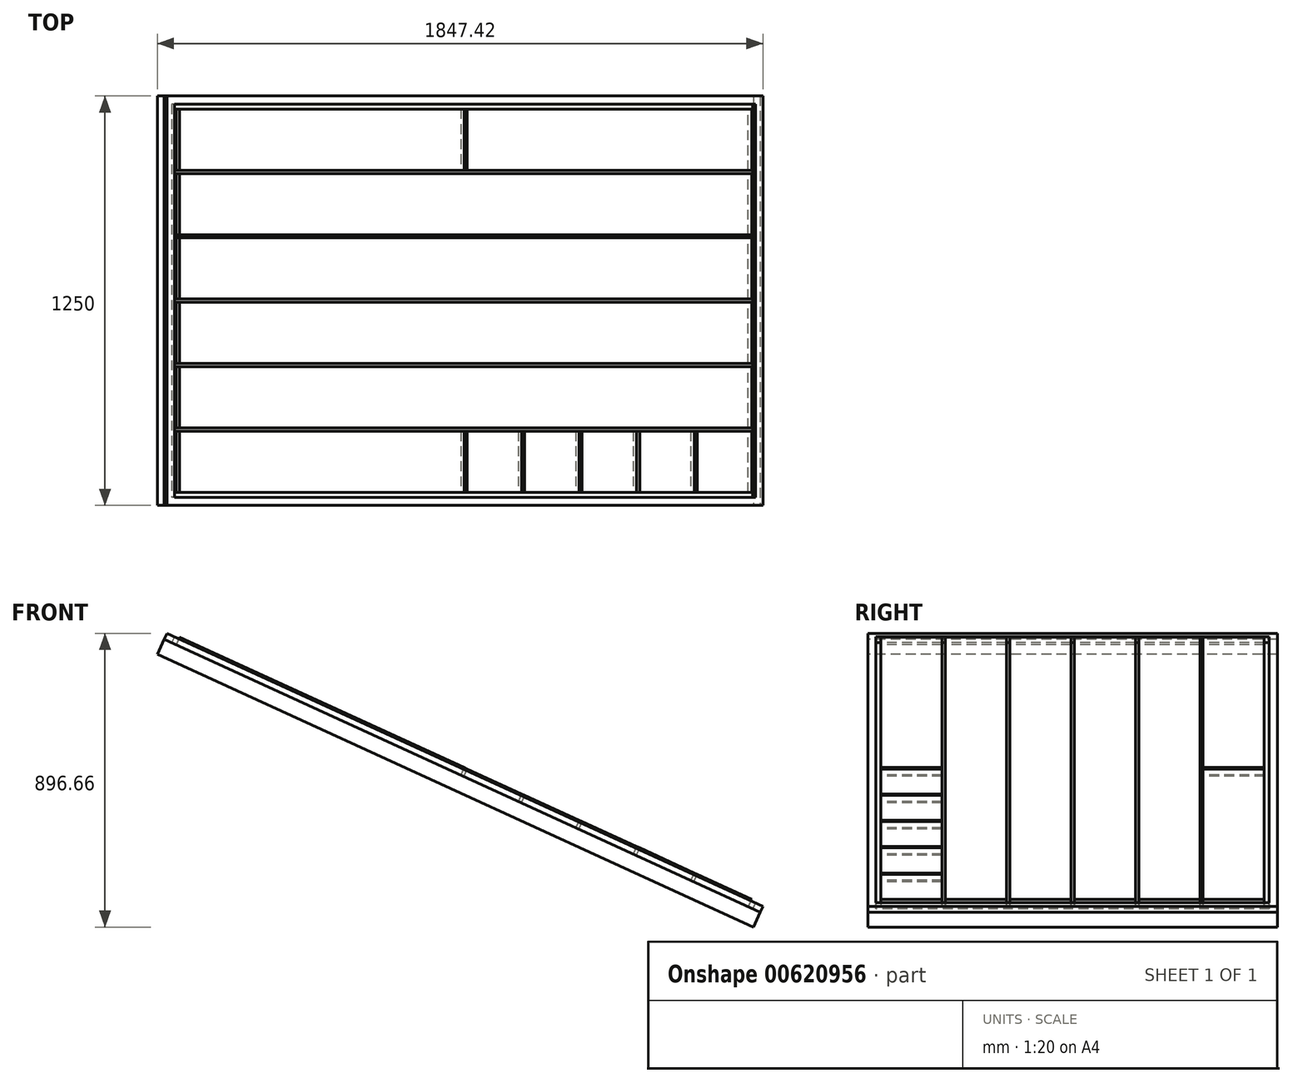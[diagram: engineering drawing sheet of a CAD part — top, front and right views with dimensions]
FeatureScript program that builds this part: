
annotation { "Feature Type Name" : "Feature", "Feature Type Description" : "" }
export const myFeature = defineFeature(function(context is Context, id is Id, definition is map)
    precondition{}
    {
        {
            var Q0;
            Q0=qCreatedBy(makeId("Front.planeOp"),FACE);
            var sketch = newSketch(context, id + "F0", { "sketchPlane" : qUnion([Q0])});
            skLineSegment(sketch, "E0", {"start": v(0, 0) * mm, "end": v(-1818.26, 833.02) * mm});
            skLineSegment(sketch, "E1.0", {"start": v(20.83, 45.46) * mm, "end": v(-1797.44, 878.48) * mm});
            skLineSegment(sketch, "E2", {"start": v(-1818.26, 833.02) * mm, "end": v(-1797.44, 878.48) * mm});
            skLineSegment(sketch, "E3", {"start": v(0, 0) * mm, "end": v(20.83, 45.46) * mm});
            skSolve(sketch);
        }
        {
            var Q0;
            Q0 = qSketchRegion(id + "F0", true);
            extrude(context, id + "F1", {"entities" : qUnion([Q0]), "oppositeDirection" : true, "depth" : 1250 * mm, "offsetDistance" : 25 * mm});
        }
        {
            var Q0;
            Q0=makeQuery(id+"F1.opExtrude","SWEPT_FACE",FACE,{"disambiguationData":[OSD([sQuery(id+"F0.wireOp",EDGE,"E1.0")])]});
            var sketch = newSketch(context, id + "F2", { "sketchPlane" : qUnion([Q0])});
            skLineSegment(sketch, "E4.0.0", {"start": v(-2000, 0) * mm, "end": v(0, 0) * mm});
            skLineSegment(sketch, "E4.0.1", {"start": v(0, 0) * mm, "end": v(0, 1250) * mm});
            skLineSegment(sketch, "E4.0.2", {"start": v(0, 1250) * mm, "end": v(-2000, 1250) * mm});
            skLineSegment(sketch, "E4.0.3", {"start": v(-2000, 1250) * mm, "end": v(-2000, 0) * mm});
            skLineSegment(sketch, "E5.0", {"start": v(-1960, 1210) * mm, "end": v(-1960, 1023.32) * mm});
            skLineSegment(sketch, "E5.1", {"start": v(-40, 1210) * mm, "end": v(-995, 1210) * mm});
            skLineSegment(sketch, "E5.2", {"start": v(-40, 40) * mm, "end": v(-40, 226.68) * mm});
            skLineSegment(sketch, "E5.3", {"start": v(-1960, 40) * mm, "end": v(-1005, 40) * mm});
            skLineSegment(sketch, "E6.0", {"start": v(-40, 630) * mm, "end": v(-1960, 630) * mm});
            skLineSegment(sketch, "E7.0", {"start": v(-40, 620) * mm, "end": v(-1960, 620) * mm});
            skLineSegment(sketch, "E8.trimOffspring", {"start": v(-1960, 620) * mm, "end": v(-1960, 433.34) * mm});
            skLineSegment(sketch, "E9.trimOffspring", {"start": v(-40, 630) * mm, "end": v(-40, 816.66) * mm});
            skLineSegment(sketch, "E10.0", {"start": v(-40, 816.66) * mm, "end": v(-1960, 816.66) * mm});
            skLineSegment(sketch, "E11.0", {"start": v(-40, 826.66) * mm, "end": v(-1960, 826.66) * mm});
            skLineSegment(sketch, "E12.0", {"start": v(-40, 1013.32) * mm, "end": v(-1960, 1013.32) * mm});
            skLineSegment(sketch, "E13.0", {"start": v(-40, 1023.32) * mm, "end": v(-1960, 1023.32) * mm});
            skLineSegment(sketch, "E14", {"start": v(-2000, 625) * mm, "end": v(-2336.37, 625) * mm, "construction": true});
            skLineSegment(sketch, "E15.MirrorCS", {"start": v(-40, 226.68) * mm, "end": v(-1960, 226.68) * mm});
            skLineSegment(sketch, "E16.MirrorCS", {"start": v(-40, 236.68) * mm, "end": v(-1960, 236.68) * mm});
            skLineSegment(sketch, "E17.MirrorCS", {"start": v(-40, 423.34) * mm, "end": v(-1960, 423.34) * mm});
            skLineSegment(sketch, "E18.MirrorCS", {"start": v(-40, 433.34) * mm, "end": v(-1960, 433.34) * mm});
            skLineSegment(sketch, "E19.trimOffspring", {"start": v(-1960, 1013.32) * mm, "end": v(-1960, 826.66) * mm});
            skLineSegment(sketch, "E20.trimOffspring", {"start": v(-1960, 816.66) * mm, "end": v(-1960, 630) * mm});
            skLineSegment(sketch, "E21.trimOffspring", {"start": v(-1960, 423.34) * mm, "end": v(-1960, 236.68) * mm});
            skLineSegment(sketch, "E22.trimOffspring", {"start": v(-1960, 226.68) * mm, "end": v(-1960, 40) * mm});
            skLineSegment(sketch, "E23.trimOffspring", {"start": v(-40, 236.68) * mm, "end": v(-40, 423.34) * mm});
            skLineSegment(sketch, "E24.trimOffspring", {"start": v(-40, 433.34) * mm, "end": v(-40, 620) * mm});
            skLineSegment(sketch, "E25.trimOffspring", {"start": v(-40, 826.66) * mm, "end": v(-40, 1013.32) * mm});
            skLineSegment(sketch, "E26.trimOffspring", {"start": v(-40, 1023.32) * mm, "end": v(-40, 1210) * mm});
            skLineSegment(sketch, "E27.0", {"start": v(-1005, 1210) * mm, "end": v(-1005, 40) * mm});
            skLineSegment(sketch, "E28.0", {"start": v(-995, 1210) * mm, "end": v(-995, 40) * mm});
            skLineSegment(sketch, "E29.trimOffspring", {"start": v(-995, 40) * mm, "end": v(-40, 40) * mm});
            skLineSegment(sketch, "E30.trimOffspring", {"start": v(-1005, 1210) * mm, "end": v(-1960, 1210) * mm});
            skLineSegment(sketch, "E31.0", {"start": v(-1188, 1210) * mm, "end": v(-1188, 40) * mm});
            skLineSegment(sketch, "E32.0", {"start": v(-1198, 1210) * mm, "end": v(-1198, 40) * mm});
            skLineSegment(sketch, "E33.0", {"start": v(-1381, 1210) * mm, "end": v(-1381, 40) * mm});
            skLineSegment(sketch, "E34.0", {"start": v(-1391, 1210) * mm, "end": v(-1391, 40) * mm});
            skLineSegment(sketch, "E35.0", {"start": v(-1574, 1210) * mm, "end": v(-1574, 40) * mm});
            skLineSegment(sketch, "E36.0", {"start": v(-1584, 1210) * mm, "end": v(-1584, 40) * mm});
            skLineSegment(sketch, "E37.0", {"start": v(-1767, 1210) * mm, "end": v(-1767, 40) * mm});
            skLineSegment(sketch, "E38.0", {"start": v(-1777, 1210) * mm, "end": v(-1777, 40) * mm});
            skLineSegment(sketch, "E39", {"start": v(-1000, 0) * mm, "end": v(-1000, -135.03) * mm, "construction": true});
            skLineSegment(sketch, "E40.MirrorCS", {"start": v(-619, 1210) * mm, "end": v(-619, 40) * mm});
            skLineSegment(sketch, "E41.MirrorCS", {"start": v(-802, 1210) * mm, "end": v(-802, 40) * mm});
            skLineSegment(sketch, "E42.MirrorCS", {"start": v(-233, 1210) * mm, "end": v(-233, 40) * mm});
            skLineSegment(sketch, "E43.MirrorCS", {"start": v(-609, 1210) * mm, "end": v(-609, 40) * mm});
            skLineSegment(sketch, "E44.MirrorCS", {"start": v(-416, 1210) * mm, "end": v(-416, 40) * mm});
            skLineSegment(sketch, "E45.MirrorCS", {"start": v(-426, 1210) * mm, "end": v(-426, 40) * mm});
            skLineSegment(sketch, "E46.MirrorCS", {"start": v(-812, 1210) * mm, "end": v(-812, 40) * mm});
            skLineSegment(sketch, "E47.MirrorCS", {"start": v(-223, 1210) * mm, "end": v(-223, 40) * mm});
            skSolve(sketch);
        }
        {
            var Q0;
            {var subQ0=sQuery(id+"F2.wireOp",EDGE,"E22.trimOffspring");Q0=makeQuery(id+"F2.imprint","IMPRINT",FACE,{"disambiguationData":[TD([[makeQuery(id+"F2.imprint","IMPRINT",EDGE,{"derivedFrom":subQ0}),1.0]])]});}
            var Q1;
            {var subQ0=sQuery(id+"F2.wireOp",EDGE,"E21.trimOffspring");Q1=makeQuery(id+"F2.imprint","IMPRINT",FACE,{"disambiguationData":[TD([[makeQuery(id+"F2.imprint","IMPRINT",EDGE,{"derivedFrom":subQ0}),1.0]])]});}
            var Q2;
            {var subQ0=sQuery(id+"F2.wireOp",EDGE,"E8.trimOffspring");Q2=makeQuery(id+"F2.imprint","IMPRINT",FACE,{"disambiguationData":[TD([[makeQuery(id+"F2.imprint","IMPRINT",EDGE,{"derivedFrom":subQ0}),1.0]])]});}
            var Q3;
            {var subQ0=sQuery(id+"F2.wireOp",EDGE,"E20.trimOffspring");Q3=makeQuery(id+"F2.imprint","IMPRINT",FACE,{"disambiguationData":[TD([[makeQuery(id+"F2.imprint","IMPRINT",EDGE,{"derivedFrom":subQ0}),1.0]])]});}
            var Q4;
            {var subQ0=sQuery(id+"F2.wireOp",EDGE,"E19.trimOffspring");Q4=makeQuery(id+"F2.imprint","IMPRINT",FACE,{"disambiguationData":[TD([[makeQuery(id+"F2.imprint","IMPRINT",EDGE,{"derivedFrom":subQ0}),1.0]])]});}
            var Q5;
            {var subQ0=sQuery(id+"F2.wireOp",EDGE,"E5.0");Q5=makeQuery(id+"F2.imprint","IMPRINT",FACE,{"disambiguationData":[TD([[makeQuery(id+"F2.imprint","IMPRINT",EDGE,{"derivedFrom":subQ0}),1.0]])]});}
            var Q6;
            {var subQ0=sQuery(id+"F2.wireOp",EDGE,"E36.0");var subQ1=sQuery(id+"F2.wireOp",EDGE,"E5.3");var subQ2=makeQuery(id+"F2.imprint","INTERSECT",VERTEX,{"derivedFrom":[subQ1,subQ0]});Q6=makeQuery(id+"F2.imprint","IMPRINT",FACE,{"disambiguationData":[TD([[makeQuery(id+"F2.imprint","IMPRINT",EDGE,{"disambiguationData":[TD([[subQ2,1.0]])],"derivedFrom":subQ1}),1.0]])]});}
            var Q7;
            {var subQ0=sQuery(id+"F2.wireOp",EDGE,"E36.0");var subQ1=sQuery(id+"F2.wireOp",EDGE,"E16.MirrorCS");var subQ2=makeQuery(id+"F2.imprint","INTERSECT",VERTEX,{"derivedFrom":[subQ1,subQ0]});Q7=makeQuery(id+"F2.imprint","IMPRINT",FACE,{"disambiguationData":[TD([[makeQuery(id+"F2.imprint","IMPRINT",EDGE,{"disambiguationData":[TD([[subQ2,-1.0]])],"derivedFrom":subQ1}),-1.0]])]});}
            var Q8;
            {var subQ0=sQuery(id+"F2.wireOp",EDGE,"E36.0");var subQ1=sQuery(id+"F2.wireOp",EDGE,"E7.0");var subQ2=makeQuery(id+"F2.imprint","INTERSECT",VERTEX,{"derivedFrom":[subQ1,subQ0]});Q8=makeQuery(id+"F2.imprint","IMPRINT",FACE,{"disambiguationData":[TD([[makeQuery(id+"F2.imprint","IMPRINT",EDGE,{"disambiguationData":[TD([[subQ2,-1.0]])],"derivedFrom":subQ1}),1.0]])]});}
            var Q9;
            {var subQ0=sQuery(id+"F2.wireOp",EDGE,"E36.0");var subQ1=sQuery(id+"F2.wireOp",EDGE,"E6.0");var subQ2=makeQuery(id+"F2.imprint","INTERSECT",VERTEX,{"derivedFrom":[subQ1,subQ0]});Q9=makeQuery(id+"F2.imprint","IMPRINT",FACE,{"disambiguationData":[TD([[makeQuery(id+"F2.imprint","IMPRINT",EDGE,{"disambiguationData":[TD([[subQ2,-1.0]])],"derivedFrom":subQ1}),-1.0]])]});}
            var Q10;
            {var subQ0=sQuery(id+"F2.wireOp",EDGE,"E36.0");var subQ1=sQuery(id+"F2.wireOp",EDGE,"E11.0");var subQ2=makeQuery(id+"F2.imprint","INTERSECT",VERTEX,{"derivedFrom":[subQ1,subQ0]});Q10=makeQuery(id+"F2.imprint","IMPRINT",FACE,{"disambiguationData":[TD([[makeQuery(id+"F2.imprint","IMPRINT",EDGE,{"disambiguationData":[TD([[subQ2,-1.0]])],"derivedFrom":subQ1}),-1.0]])]});}
            var Q11;
            {var subQ0=sQuery(id+"F2.wireOp",EDGE,"E36.0");var subQ1=sQuery(id+"F2.wireOp",EDGE,"E13.0");var subQ2=makeQuery(id+"F2.imprint","INTERSECT",VERTEX,{"derivedFrom":[subQ1,subQ0]});Q11=makeQuery(id+"F2.imprint","IMPRINT",FACE,{"disambiguationData":[TD([[makeQuery(id+"F2.imprint","IMPRINT",EDGE,{"disambiguationData":[TD([[subQ2,-1.0]])],"derivedFrom":subQ1}),-1.0]])]});}
            var Q12;
            {var subQ0=sQuery(id+"F2.wireOp",EDGE,"E34.0");var subQ1=sQuery(id+"F2.wireOp",EDGE,"E13.0");var subQ2=makeQuery(id+"F2.imprint","INTERSECT",VERTEX,{"derivedFrom":[subQ1,subQ0]});Q12=makeQuery(id+"F2.imprint","IMPRINT",FACE,{"disambiguationData":[TD([[makeQuery(id+"F2.imprint","IMPRINT",EDGE,{"disambiguationData":[TD([[subQ2,-1.0]])],"derivedFrom":subQ1}),-1.0]])]});}
            var Q13;
            {var subQ0=sQuery(id+"F2.wireOp",EDGE,"E34.0");var subQ1=sQuery(id+"F2.wireOp",EDGE,"E11.0");var subQ2=makeQuery(id+"F2.imprint","INTERSECT",VERTEX,{"derivedFrom":[subQ1,subQ0]});Q13=makeQuery(id+"F2.imprint","IMPRINT",FACE,{"disambiguationData":[TD([[makeQuery(id+"F2.imprint","IMPRINT",EDGE,{"disambiguationData":[TD([[subQ2,-1.0]])],"derivedFrom":subQ1}),-1.0]])]});}
            var Q14;
            {var subQ0=sQuery(id+"F2.wireOp",EDGE,"E34.0");var subQ1=sQuery(id+"F2.wireOp",EDGE,"E6.0");var subQ2=makeQuery(id+"F2.imprint","INTERSECT",VERTEX,{"derivedFrom":[subQ1,subQ0]});Q14=makeQuery(id+"F2.imprint","IMPRINT",FACE,{"disambiguationData":[TD([[makeQuery(id+"F2.imprint","IMPRINT",EDGE,{"disambiguationData":[TD([[subQ2,-1.0]])],"derivedFrom":subQ1}),-1.0]])]});}
            var Q15;
            {var subQ0=sQuery(id+"F2.wireOp",EDGE,"E34.0");var subQ1=sQuery(id+"F2.wireOp",EDGE,"E7.0");var subQ2=makeQuery(id+"F2.imprint","INTERSECT",VERTEX,{"derivedFrom":[subQ1,subQ0]});Q15=makeQuery(id+"F2.imprint","IMPRINT",FACE,{"disambiguationData":[TD([[makeQuery(id+"F2.imprint","IMPRINT",EDGE,{"disambiguationData":[TD([[subQ2,-1.0]])],"derivedFrom":subQ1}),1.0]])]});}
            var Q16;
            {var subQ0=sQuery(id+"F2.wireOp",EDGE,"E34.0");var subQ1=sQuery(id+"F2.wireOp",EDGE,"E16.MirrorCS");var subQ2=makeQuery(id+"F2.imprint","INTERSECT",VERTEX,{"derivedFrom":[subQ1,subQ0]});Q16=makeQuery(id+"F2.imprint","IMPRINT",FACE,{"disambiguationData":[TD([[makeQuery(id+"F2.imprint","IMPRINT",EDGE,{"disambiguationData":[TD([[subQ2,-1.0]])],"derivedFrom":subQ1}),-1.0]])]});}
            var Q17;
            {var subQ0=sQuery(id+"F2.wireOp",EDGE,"E34.0");var subQ1=sQuery(id+"F2.wireOp",EDGE,"E5.3");var subQ2=makeQuery(id+"F2.imprint","INTERSECT",VERTEX,{"derivedFrom":[subQ1,subQ0]});Q17=makeQuery(id+"F2.imprint","IMPRINT",FACE,{"disambiguationData":[TD([[makeQuery(id+"F2.imprint","IMPRINT",EDGE,{"disambiguationData":[TD([[subQ2,1.0]])],"derivedFrom":subQ1}),1.0]])]});}
            var Q18;
            {var subQ0=sQuery(id+"F2.wireOp",EDGE,"E32.0");var subQ1=sQuery(id+"F2.wireOp",EDGE,"E5.3");var subQ2=makeQuery(id+"F2.imprint","INTERSECT",VERTEX,{"derivedFrom":[subQ1,subQ0]});Q18=makeQuery(id+"F2.imprint","IMPRINT",FACE,{"disambiguationData":[TD([[makeQuery(id+"F2.imprint","IMPRINT",EDGE,{"disambiguationData":[TD([[subQ2,1.0]])],"derivedFrom":subQ1}),1.0]])]});}
            var Q19;
            {var subQ0=sQuery(id+"F2.wireOp",EDGE,"E32.0");var subQ1=sQuery(id+"F2.wireOp",EDGE,"E16.MirrorCS");var subQ2=makeQuery(id+"F2.imprint","INTERSECT",VERTEX,{"derivedFrom":[subQ1,subQ0]});Q19=makeQuery(id+"F2.imprint","IMPRINT",FACE,{"disambiguationData":[TD([[makeQuery(id+"F2.imprint","IMPRINT",EDGE,{"disambiguationData":[TD([[subQ2,-1.0]])],"derivedFrom":subQ1}),-1.0]])]});}
            var Q20;
            {var subQ0=sQuery(id+"F2.wireOp",EDGE,"E32.0");var subQ1=sQuery(id+"F2.wireOp",EDGE,"E7.0");var subQ2=makeQuery(id+"F2.imprint","INTERSECT",VERTEX,{"derivedFrom":[subQ1,subQ0]});Q20=makeQuery(id+"F2.imprint","IMPRINT",FACE,{"disambiguationData":[TD([[makeQuery(id+"F2.imprint","IMPRINT",EDGE,{"disambiguationData":[TD([[subQ2,-1.0]])],"derivedFrom":subQ1}),1.0]])]});}
            var Q21;
            {var subQ0=sQuery(id+"F2.wireOp",EDGE,"E32.0");var subQ1=sQuery(id+"F2.wireOp",EDGE,"E6.0");var subQ2=makeQuery(id+"F2.imprint","INTERSECT",VERTEX,{"derivedFrom":[subQ1,subQ0]});Q21=makeQuery(id+"F2.imprint","IMPRINT",FACE,{"disambiguationData":[TD([[makeQuery(id+"F2.imprint","IMPRINT",EDGE,{"disambiguationData":[TD([[subQ2,-1.0]])],"derivedFrom":subQ1}),-1.0]])]});}
            var Q22;
            {var subQ0=sQuery(id+"F2.wireOp",EDGE,"E32.0");var subQ1=sQuery(id+"F2.wireOp",EDGE,"E11.0");var subQ2=makeQuery(id+"F2.imprint","INTERSECT",VERTEX,{"derivedFrom":[subQ1,subQ0]});Q22=makeQuery(id+"F2.imprint","IMPRINT",FACE,{"disambiguationData":[TD([[makeQuery(id+"F2.imprint","IMPRINT",EDGE,{"disambiguationData":[TD([[subQ2,-1.0]])],"derivedFrom":subQ1}),-1.0]])]});}
            var Q23;
            {var subQ0=sQuery(id+"F2.wireOp",EDGE,"E32.0");var subQ1=sQuery(id+"F2.wireOp",EDGE,"E13.0");var subQ2=makeQuery(id+"F2.imprint","INTERSECT",VERTEX,{"derivedFrom":[subQ1,subQ0]});Q23=makeQuery(id+"F2.imprint","IMPRINT",FACE,{"disambiguationData":[TD([[makeQuery(id+"F2.imprint","IMPRINT",EDGE,{"disambiguationData":[TD([[subQ2,-1.0]])],"derivedFrom":subQ1}),-1.0]])]});}
            var Q24;
            {var subQ0=sQuery(id+"F2.wireOp",EDGE,"E27.0");var subQ1=sQuery(id+"F2.wireOp",EDGE,"E5.3");var subQ2=makeQuery(id+"F2.imprint","INTERSECT",VERTEX,{"derivedFrom":[subQ1,subQ0]});Q24=makeQuery(id+"F2.imprint","IMPRINT",FACE,{"disambiguationData":[TD([[makeQuery(id+"F2.imprint","IMPRINT",EDGE,{"disambiguationData":[TD([[subQ2,1.0]])],"derivedFrom":subQ1}),1.0]])]});}
            var Q25;
            {var subQ0=sQuery(id+"F2.wireOp",EDGE,"E27.0");var subQ1=sQuery(id+"F2.wireOp",EDGE,"E16.MirrorCS");var subQ2=makeQuery(id+"F2.imprint","INTERSECT",VERTEX,{"derivedFrom":[subQ1,subQ0]});Q25=makeQuery(id+"F2.imprint","IMPRINT",FACE,{"disambiguationData":[TD([[makeQuery(id+"F2.imprint","IMPRINT",EDGE,{"disambiguationData":[TD([[subQ2,-1.0]])],"derivedFrom":subQ1}),-1.0]])]});}
            var Q26;
            {var subQ0=sQuery(id+"F2.wireOp",EDGE,"E27.0");var subQ1=sQuery(id+"F2.wireOp",EDGE,"E7.0");var subQ2=makeQuery(id+"F2.imprint","INTERSECT",VERTEX,{"derivedFrom":[subQ1,subQ0]});Q26=makeQuery(id+"F2.imprint","IMPRINT",FACE,{"disambiguationData":[TD([[makeQuery(id+"F2.imprint","IMPRINT",EDGE,{"disambiguationData":[TD([[subQ2,-1.0]])],"derivedFrom":subQ1}),1.0]])]});}
            var Q27;
            {var subQ0=sQuery(id+"F2.wireOp",EDGE,"E27.0");var subQ1=sQuery(id+"F2.wireOp",EDGE,"E6.0");var subQ2=makeQuery(id+"F2.imprint","INTERSECT",VERTEX,{"derivedFrom":[subQ1,subQ0]});Q27=makeQuery(id+"F2.imprint","IMPRINT",FACE,{"disambiguationData":[TD([[makeQuery(id+"F2.imprint","IMPRINT",EDGE,{"disambiguationData":[TD([[subQ2,-1.0]])],"derivedFrom":subQ1}),-1.0]])]});}
            var Q28;
            {var subQ0=sQuery(id+"F2.wireOp",EDGE,"E27.0");var subQ1=sQuery(id+"F2.wireOp",EDGE,"E11.0");var subQ2=makeQuery(id+"F2.imprint","INTERSECT",VERTEX,{"derivedFrom":[subQ1,subQ0]});Q28=makeQuery(id+"F2.imprint","IMPRINT",FACE,{"disambiguationData":[TD([[makeQuery(id+"F2.imprint","IMPRINT",EDGE,{"disambiguationData":[TD([[subQ2,-1.0]])],"derivedFrom":subQ1}),-1.0]])]});}
            var Q29;
            {var subQ0=sQuery(id+"F2.wireOp",EDGE,"E27.0");var subQ1=sQuery(id+"F2.wireOp",EDGE,"E13.0");var subQ2=makeQuery(id+"F2.imprint","INTERSECT",VERTEX,{"derivedFrom":[subQ1,subQ0]});Q29=makeQuery(id+"F2.imprint","IMPRINT",FACE,{"disambiguationData":[TD([[makeQuery(id+"F2.imprint","IMPRINT",EDGE,{"disambiguationData":[TD([[subQ2,-1.0]])],"derivedFrom":subQ1}),-1.0]])]});}
            var Q30;
            {var subQ0=sQuery(id+"F2.wireOp",EDGE,"E46.MirrorCS");var subQ1=sQuery(id+"F2.wireOp",EDGE,"E15.MirrorCS");var subQ2=makeQuery(id+"F2.imprint","INTERSECT",VERTEX,{"derivedFrom":[subQ1,subQ0]});Q30=makeQuery(id+"F2.imprint","IMPRINT",FACE,{"disambiguationData":[TD([[makeQuery(id+"F2.imprint","IMPRINT",EDGE,{"disambiguationData":[TD([[subQ2,-1.0]])],"derivedFrom":subQ1}),1.0]])]});}
            var Q31;
            {var subQ0=sQuery(id+"F2.wireOp",EDGE,"E46.MirrorCS");var subQ1=sQuery(id+"F2.wireOp",EDGE,"E16.MirrorCS");var subQ2=makeQuery(id+"F2.imprint","INTERSECT",VERTEX,{"derivedFrom":[subQ1,subQ0]});Q31=makeQuery(id+"F2.imprint","IMPRINT",FACE,{"disambiguationData":[TD([[makeQuery(id+"F2.imprint","IMPRINT",EDGE,{"disambiguationData":[TD([[subQ2,-1.0]])],"derivedFrom":subQ1}),-1.0]])]});}
            var Q32;
            {var subQ0=sQuery(id+"F2.wireOp",EDGE,"E46.MirrorCS");var subQ1=sQuery(id+"F2.wireOp",EDGE,"E7.0");var subQ2=makeQuery(id+"F2.imprint","INTERSECT",VERTEX,{"derivedFrom":[subQ1,subQ0]});Q32=makeQuery(id+"F2.imprint","IMPRINT",FACE,{"disambiguationData":[TD([[makeQuery(id+"F2.imprint","IMPRINT",EDGE,{"disambiguationData":[TD([[subQ2,-1.0]])],"derivedFrom":subQ1}),1.0]])]});}
            var Q33;
            {var subQ0=sQuery(id+"F2.wireOp",EDGE,"E46.MirrorCS");var subQ1=sQuery(id+"F2.wireOp",EDGE,"E6.0");var subQ2=makeQuery(id+"F2.imprint","INTERSECT",VERTEX,{"derivedFrom":[subQ1,subQ0]});Q33=makeQuery(id+"F2.imprint","IMPRINT",FACE,{"disambiguationData":[TD([[makeQuery(id+"F2.imprint","IMPRINT",EDGE,{"disambiguationData":[TD([[subQ2,-1.0]])],"derivedFrom":subQ1}),-1.0]])]});}
            var Q34;
            {var subQ0=sQuery(id+"F2.wireOp",EDGE,"E46.MirrorCS");var subQ1=sQuery(id+"F2.wireOp",EDGE,"E11.0");var subQ2=makeQuery(id+"F2.imprint","INTERSECT",VERTEX,{"derivedFrom":[subQ1,subQ0]});Q34=makeQuery(id+"F2.imprint","IMPRINT",FACE,{"disambiguationData":[TD([[makeQuery(id+"F2.imprint","IMPRINT",EDGE,{"disambiguationData":[TD([[subQ2,-1.0]])],"derivedFrom":subQ1}),-1.0]])]});}
            var Q35;
            {var subQ0=sQuery(id+"F2.wireOp",EDGE,"E28.0");var subQ1=sQuery(id+"F2.wireOp",EDGE,"E5.1");var subQ2=makeQuery(id+"F2.imprint","INTERSECT",VERTEX,{"derivedFrom":[subQ1,subQ0]});Q35=makeQuery(id+"F2.imprint","IMPRINT",FACE,{"disambiguationData":[TD([[makeQuery(id+"F2.imprint","IMPRINT",EDGE,{"disambiguationData":[TD([[subQ2,1.0]])],"derivedFrom":subQ1}),1.0]])]});}
            var Q36;
            {var subQ0=sQuery(id+"F2.wireOp",EDGE,"E40.MirrorCS");var subQ1=sQuery(id+"F2.wireOp",EDGE,"E5.1");var subQ2=makeQuery(id+"F2.imprint","INTERSECT",VERTEX,{"derivedFrom":[subQ1,subQ0]});Q36=makeQuery(id+"F2.imprint","IMPRINT",FACE,{"disambiguationData":[TD([[makeQuery(id+"F2.imprint","IMPRINT",EDGE,{"disambiguationData":[TD([[subQ2,-1.0]])],"derivedFrom":subQ1}),1.0]])]});}
            var Q37;
            {var subQ0=sQuery(id+"F2.wireOp",EDGE,"E40.MirrorCS");var subQ1=sQuery(id+"F2.wireOp",EDGE,"E11.0");var subQ2=makeQuery(id+"F2.imprint","INTERSECT",VERTEX,{"derivedFrom":[subQ1,subQ0]});Q37=makeQuery(id+"F2.imprint","IMPRINT",FACE,{"disambiguationData":[TD([[makeQuery(id+"F2.imprint","IMPRINT",EDGE,{"disambiguationData":[TD([[subQ2,-1.0]])],"derivedFrom":subQ1}),-1.0]])]});}
            var Q38;
            {var subQ0=sQuery(id+"F2.wireOp",EDGE,"E40.MirrorCS");var subQ1=sQuery(id+"F2.wireOp",EDGE,"E6.0");var subQ2=makeQuery(id+"F2.imprint","INTERSECT",VERTEX,{"derivedFrom":[subQ1,subQ0]});Q38=makeQuery(id+"F2.imprint","IMPRINT",FACE,{"disambiguationData":[TD([[makeQuery(id+"F2.imprint","IMPRINT",EDGE,{"disambiguationData":[TD([[subQ2,-1.0]])],"derivedFrom":subQ1}),-1.0]])]});}
            var Q39;
            {var subQ0=sQuery(id+"F2.wireOp",EDGE,"E40.MirrorCS");var subQ1=sQuery(id+"F2.wireOp",EDGE,"E7.0");var subQ2=makeQuery(id+"F2.imprint","INTERSECT",VERTEX,{"derivedFrom":[subQ1,subQ0]});Q39=makeQuery(id+"F2.imprint","IMPRINT",FACE,{"disambiguationData":[TD([[makeQuery(id+"F2.imprint","IMPRINT",EDGE,{"disambiguationData":[TD([[subQ2,-1.0]])],"derivedFrom":subQ1}),1.0]])]});}
            var Q40;
            {var subQ0=sQuery(id+"F2.wireOp",EDGE,"E40.MirrorCS");var subQ1=sQuery(id+"F2.wireOp",EDGE,"E16.MirrorCS");var subQ2=makeQuery(id+"F2.imprint","INTERSECT",VERTEX,{"derivedFrom":[subQ1,subQ0]});Q40=makeQuery(id+"F2.imprint","IMPRINT",FACE,{"disambiguationData":[TD([[makeQuery(id+"F2.imprint","IMPRINT",EDGE,{"disambiguationData":[TD([[subQ2,-1.0]])],"derivedFrom":subQ1}),-1.0]])]});}
            var Q41;
            {var subQ0=sQuery(id+"F2.wireOp",EDGE,"E40.MirrorCS");var subQ1=sQuery(id+"F2.wireOp",EDGE,"E15.MirrorCS");var subQ2=makeQuery(id+"F2.imprint","INTERSECT",VERTEX,{"derivedFrom":[subQ1,subQ0]});Q41=makeQuery(id+"F2.imprint","IMPRINT",FACE,{"disambiguationData":[TD([[makeQuery(id+"F2.imprint","IMPRINT",EDGE,{"disambiguationData":[TD([[subQ2,-1.0]])],"derivedFrom":subQ1}),1.0]])]});}
            var Q42;
            {var subQ0=sQuery(id+"F2.wireOp",EDGE,"E45.MirrorCS");var subQ1=sQuery(id+"F2.wireOp",EDGE,"E15.MirrorCS");var subQ2=makeQuery(id+"F2.imprint","INTERSECT",VERTEX,{"derivedFrom":[subQ1,subQ0]});Q42=makeQuery(id+"F2.imprint","IMPRINT",FACE,{"disambiguationData":[TD([[makeQuery(id+"F2.imprint","IMPRINT",EDGE,{"disambiguationData":[TD([[subQ2,-1.0]])],"derivedFrom":subQ1}),1.0]])]});}
            var Q43;
            {var subQ0=sQuery(id+"F2.wireOp",EDGE,"E45.MirrorCS");var subQ1=sQuery(id+"F2.wireOp",EDGE,"E16.MirrorCS");var subQ2=makeQuery(id+"F2.imprint","INTERSECT",VERTEX,{"derivedFrom":[subQ1,subQ0]});Q43=makeQuery(id+"F2.imprint","IMPRINT",FACE,{"disambiguationData":[TD([[makeQuery(id+"F2.imprint","IMPRINT",EDGE,{"disambiguationData":[TD([[subQ2,-1.0]])],"derivedFrom":subQ1}),-1.0]])]});}
            var Q44;
            {var subQ0=sQuery(id+"F2.wireOp",EDGE,"E45.MirrorCS");var subQ1=sQuery(id+"F2.wireOp",EDGE,"E7.0");var subQ2=makeQuery(id+"F2.imprint","INTERSECT",VERTEX,{"derivedFrom":[subQ1,subQ0]});Q44=makeQuery(id+"F2.imprint","IMPRINT",FACE,{"disambiguationData":[TD([[makeQuery(id+"F2.imprint","IMPRINT",EDGE,{"disambiguationData":[TD([[subQ2,-1.0]])],"derivedFrom":subQ1}),1.0]])]});}
            var Q45;
            {var subQ0=sQuery(id+"F2.wireOp",EDGE,"E45.MirrorCS");var subQ1=sQuery(id+"F2.wireOp",EDGE,"E6.0");var subQ2=makeQuery(id+"F2.imprint","INTERSECT",VERTEX,{"derivedFrom":[subQ1,subQ0]});Q45=makeQuery(id+"F2.imprint","IMPRINT",FACE,{"disambiguationData":[TD([[makeQuery(id+"F2.imprint","IMPRINT",EDGE,{"disambiguationData":[TD([[subQ2,-1.0]])],"derivedFrom":subQ1}),-1.0]])]});}
            var Q46;
            {var subQ0=sQuery(id+"F2.wireOp",EDGE,"E45.MirrorCS");var subQ1=sQuery(id+"F2.wireOp",EDGE,"E11.0");var subQ2=makeQuery(id+"F2.imprint","INTERSECT",VERTEX,{"derivedFrom":[subQ1,subQ0]});Q46=makeQuery(id+"F2.imprint","IMPRINT",FACE,{"disambiguationData":[TD([[makeQuery(id+"F2.imprint","IMPRINT",EDGE,{"disambiguationData":[TD([[subQ2,-1.0]])],"derivedFrom":subQ1}),-1.0]])]});}
            var Q47;
            {var subQ0=sQuery(id+"F2.wireOp",EDGE,"E43.MirrorCS");var subQ1=sQuery(id+"F2.wireOp",EDGE,"E5.1");var subQ2=makeQuery(id+"F2.imprint","INTERSECT",VERTEX,{"derivedFrom":[subQ1,subQ0]});Q47=makeQuery(id+"F2.imprint","IMPRINT",FACE,{"disambiguationData":[TD([[makeQuery(id+"F2.imprint","IMPRINT",EDGE,{"disambiguationData":[TD([[subQ2,1.0]])],"derivedFrom":subQ1}),1.0]])]});}
            var Q48;
            {var subQ0=sQuery(id+"F2.wireOp",EDGE,"E42.MirrorCS");var subQ1=sQuery(id+"F2.wireOp",EDGE,"E5.1");var subQ2=makeQuery(id+"F2.imprint","INTERSECT",VERTEX,{"derivedFrom":[subQ1,subQ0]});Q48=makeQuery(id+"F2.imprint","IMPRINT",FACE,{"disambiguationData":[TD([[makeQuery(id+"F2.imprint","IMPRINT",EDGE,{"disambiguationData":[TD([[subQ2,-1.0]])],"derivedFrom":subQ1}),1.0]])]});}
            var Q49;
            {var subQ0=sQuery(id+"F2.wireOp",EDGE,"E42.MirrorCS");var subQ1=sQuery(id+"F2.wireOp",EDGE,"E11.0");var subQ2=makeQuery(id+"F2.imprint","INTERSECT",VERTEX,{"derivedFrom":[subQ1,subQ0]});Q49=makeQuery(id+"F2.imprint","IMPRINT",FACE,{"disambiguationData":[TD([[makeQuery(id+"F2.imprint","IMPRINT",EDGE,{"disambiguationData":[TD([[subQ2,-1.0]])],"derivedFrom":subQ1}),-1.0]])]});}
            var Q50;
            {var subQ0=sQuery(id+"F2.wireOp",EDGE,"E42.MirrorCS");var subQ1=sQuery(id+"F2.wireOp",EDGE,"E6.0");var subQ2=makeQuery(id+"F2.imprint","INTERSECT",VERTEX,{"derivedFrom":[subQ1,subQ0]});Q50=makeQuery(id+"F2.imprint","IMPRINT",FACE,{"disambiguationData":[TD([[makeQuery(id+"F2.imprint","IMPRINT",EDGE,{"disambiguationData":[TD([[subQ2,-1.0]])],"derivedFrom":subQ1}),-1.0]])]});}
            var Q51;
            {var subQ0=sQuery(id+"F2.wireOp",EDGE,"E42.MirrorCS");var subQ1=sQuery(id+"F2.wireOp",EDGE,"E7.0");var subQ2=makeQuery(id+"F2.imprint","INTERSECT",VERTEX,{"derivedFrom":[subQ1,subQ0]});Q51=makeQuery(id+"F2.imprint","IMPRINT",FACE,{"disambiguationData":[TD([[makeQuery(id+"F2.imprint","IMPRINT",EDGE,{"disambiguationData":[TD([[subQ2,-1.0]])],"derivedFrom":subQ1}),1.0]])]});}
            var Q52;
            {var subQ0=sQuery(id+"F2.wireOp",EDGE,"E42.MirrorCS");var subQ1=sQuery(id+"F2.wireOp",EDGE,"E16.MirrorCS");var subQ2=makeQuery(id+"F2.imprint","INTERSECT",VERTEX,{"derivedFrom":[subQ1,subQ0]});Q52=makeQuery(id+"F2.imprint","IMPRINT",FACE,{"disambiguationData":[TD([[makeQuery(id+"F2.imprint","IMPRINT",EDGE,{"disambiguationData":[TD([[subQ2,-1.0]])],"derivedFrom":subQ1}),-1.0]])]});}
            var Q53;
            {var subQ0=sQuery(id+"F2.wireOp",EDGE,"E42.MirrorCS");var subQ1=sQuery(id+"F2.wireOp",EDGE,"E15.MirrorCS");var subQ2=makeQuery(id+"F2.imprint","INTERSECT",VERTEX,{"derivedFrom":[subQ1,subQ0]});Q53=makeQuery(id+"F2.imprint","IMPRINT",FACE,{"disambiguationData":[TD([[makeQuery(id+"F2.imprint","IMPRINT",EDGE,{"disambiguationData":[TD([[subQ2,-1.0]])],"derivedFrom":subQ1}),1.0]])]});}
            var Q54;
            {var subQ0=sQuery(id+"F2.wireOp",EDGE,"E5.2");Q54=makeQuery(id+"F2.imprint","IMPRINT",FACE,{"disambiguationData":[TD([[makeQuery(id+"F2.imprint","IMPRINT",EDGE,{"derivedFrom":subQ0}),1.0]])]});}
            var Q55;
            {var subQ0=sQuery(id+"F2.wireOp",EDGE,"E23.trimOffspring");Q55=makeQuery(id+"F2.imprint","IMPRINT",FACE,{"disambiguationData":[TD([[makeQuery(id+"F2.imprint","IMPRINT",EDGE,{"derivedFrom":subQ0}),1.0]])]});}
            var Q56;
            {var subQ0=sQuery(id+"F2.wireOp",EDGE,"E24.trimOffspring");Q56=makeQuery(id+"F2.imprint","IMPRINT",FACE,{"disambiguationData":[TD([[makeQuery(id+"F2.imprint","IMPRINT",EDGE,{"derivedFrom":subQ0}),1.0]])]});}
            var Q57;
            {var subQ0=sQuery(id+"F2.wireOp",EDGE,"E9.trimOffspring");Q57=makeQuery(id+"F2.imprint","IMPRINT",FACE,{"disambiguationData":[TD([[makeQuery(id+"F2.imprint","IMPRINT",EDGE,{"derivedFrom":subQ0}),1.0]])]});}
            var Q58;
            {var subQ0=sQuery(id+"F2.wireOp",EDGE,"E25.trimOffspring");Q58=makeQuery(id+"F2.imprint","IMPRINT",FACE,{"disambiguationData":[TD([[makeQuery(id+"F2.imprint","IMPRINT",EDGE,{"derivedFrom":subQ0}),1.0]])]});}
            var Q59;
            {var subQ0=sQuery(id+"F2.wireOp",EDGE,"E26.trimOffspring");Q59=makeQuery(id+"F2.imprint","IMPRINT",FACE,{"disambiguationData":[TD([[makeQuery(id+"F2.imprint","IMPRINT",EDGE,{"derivedFrom":subQ0}),1.0]])]});}
            extrude(context, id + "F3", {"entities" : qUnion([Q0, Q1, Q2, Q3, Q4, Q5, Q6, Q7, Q8, Q9, Q10, Q11, Q12, Q13, Q14, Q15, Q16, Q17, Q18, Q19, Q20, Q21, Q22, Q23, Q24, Q25, Q26, Q27, Q28, Q29, Q30, Q31, Q32, Q33, Q34, Q35, Q36, Q37, Q38, Q39, Q40, Q41, Q42, Q43, Q44, Q45, Q46, Q47, Q48, Q49, Q50, Q51, Q52, Q53, Q54, Q55, Q56, Q57, Q58, Q59]), "operationType" : NewBodyOperationType.ADD, "depth" : 25 * mm, "offsetDistance" : 25 * mm});
        }
        {
            var Q0;
            Q0=makeQuery(id+"F1.opExtrude","SWEPT_FACE",FACE,{"disambiguationData":[OSD([sQuery(id+"F0.wireOp",EDGE,"E1.0")])]});
            var sketch = newSketch(context, id + "F4", { "sketchPlane" : qUnion([Q0])});
            skLineSegment(sketch, "E48.0", {"start": v(-2000, 1250) * mm, "end": v(-2000, 0) * mm});
            skLineSegment(sketch, "E49.0", {"start": v(0, 0) * mm, "end": v(-2000, 0) * mm});
            skLineSegment(sketch, "E50.0", {"start": v(0, 1250) * mm, "end": v(-2000, 1250) * mm});
            skLineSegment(sketch, "E51.0", {"start": v(0, 1250) * mm, "end": v(0, 0) * mm});
            skLineSegment(sketch, "E52.0", {"start": v(-25, 1225) * mm, "end": v(-1975, 1225) * mm});
            skLineSegment(sketch, "E52.1", {"start": v(-25, 1225) * mm, "end": v(-25, 25) * mm});
            skLineSegment(sketch, "E52.2", {"start": v(-25, 25) * mm, "end": v(-1975, 25) * mm});
            skLineSegment(sketch, "E52.3", {"start": v(-1975, 1225) * mm, "end": v(-1975, 25) * mm});
            skSolve(sketch);
        }
        {
            var Q0;
            Q0=makeQuery(id+"F4.imprint","IMPRINT",FACE,{"disambiguationData":[TD([[makeQuery(id+"F4.imprint","IMPRINT",EDGE,{"derivedFrom":sQuery(id+"F4.wireOp",EDGE,"E48.0")}),1.0]])]});
            extrude(context, id + "F5", {"entities" : qUnion([Q0]), "depth" : 20 * mm, "offsetDistance" : 25 * mm});
        }
    });
